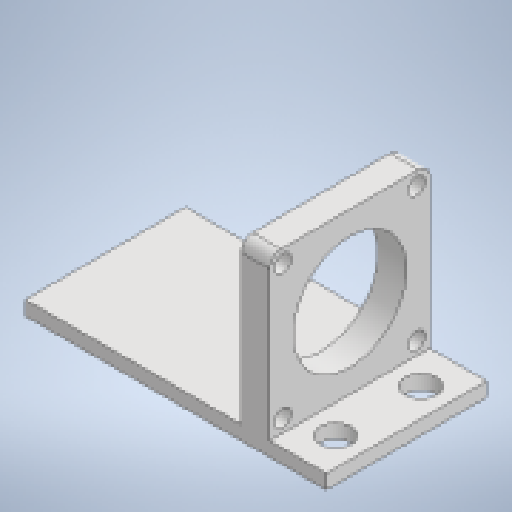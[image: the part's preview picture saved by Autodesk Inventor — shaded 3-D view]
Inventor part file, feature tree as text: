
AUTODESK INVENTOR PART (.ipt)
format: ipt  version: 2023 (Build 270158000, 158)  size: 170,496 bytes
history: native  units: mm
features: extrude x2, sketch x2
ambient origin geometry x8: Origin, YZ Plane, XZ Plane, XY Plane, X Axis, Y Axis, Z Axis, Center Point
bodies: Solid1 (feature_tree)
feature tree (4):
  extrude  "Extrusion1"  Depth=56.4mm
  extrude  "Extrusion2"  Depth=5.0mm
  sketch  "Sketch1"  dims[d0=56.4mm d1=47.14mm]
  sketch  "Sketch2"  dims[d2=40.0mm d3=6.0mm d4=4.0mm d5=4.0mm d6=10.0mm d7=0.0mm d8=30.0mm d9=76.0mm d10=11.0mm d11=11.0mm d12=30.0mm d14=5.0mm d15=0.0mm]
